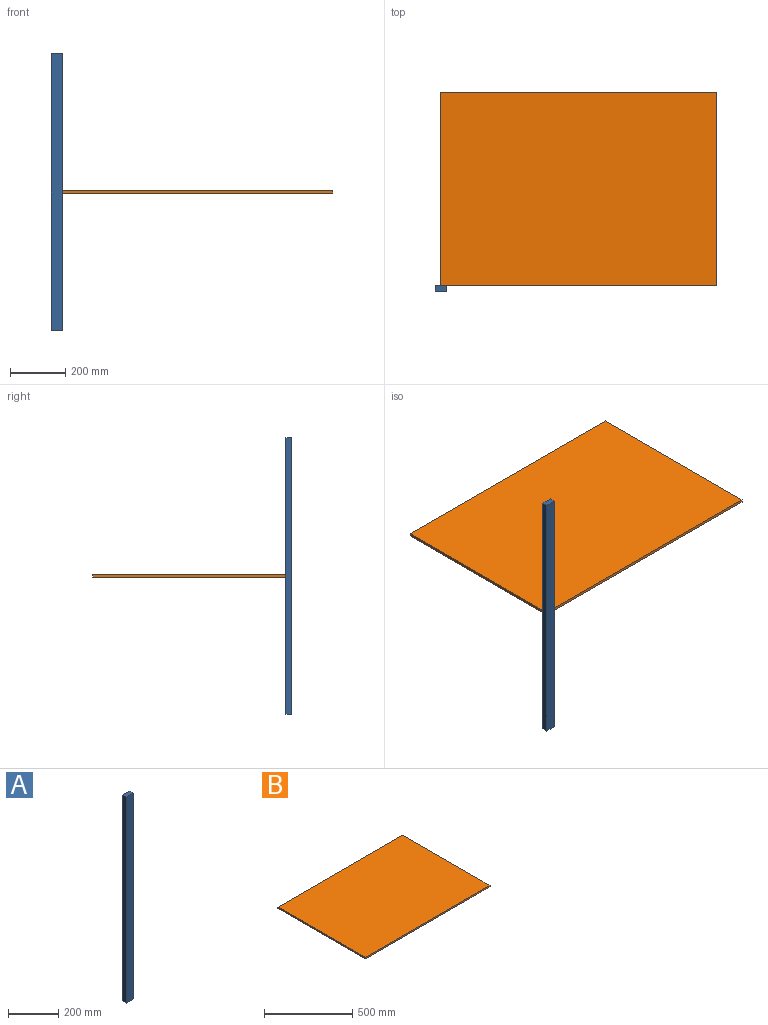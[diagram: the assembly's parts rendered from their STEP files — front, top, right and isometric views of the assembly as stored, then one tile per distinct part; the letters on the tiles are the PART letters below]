
ASSEMBLY  parts=2 mates=1
PART A: 6 faces, bbox 40x20x1000 mm
  f0: plane 1000x20mm, normal (1,0,0), area 20000mm2, adj f1,f3,f4,f5
  f1: plane 40x20mm, normal (0,0,1), area 800mm2, adj f0,f2,f4,f5
  f2: plane 1000x20mm, normal (-1,0,0), area 20000mm2, adj f1,f3,f4,f5
  f3: plane 40x20mm, normal (0,0,-1), area 800mm2, adj f0,f2,f4,f5
  f4: plane 1000x40mm, normal (0,-1,0), area 40000mm2, adj f0,f1,f2,f3
  f5: plane 1000x40mm, normal (0,1,0), area 40000mm2, adj f0,f1,f2,f3
PART B: 6 faces, bbox 1000x700x10 mm
  f0: plane 700x10mm, normal (1,0,0), area 7000mm2, adj f1,f3,f4,f5
  f1: plane 1000x10mm, normal (0,1,0), area 10000mm2, adj f0,f2,f4,f5
  f2: plane 700x10mm, normal (-1,0,0), area 7000mm2, adj f1,f3,f4,f5
  f3: plane 1000x10mm, normal (0,-1,0), area 10000mm2, adj f0,f2,f4,f5
  f4: plane 1000x700mm, normal (0,0,1), area 700000mm2, adj f0,f1,f2,f3
  f5: plane 1000x700mm, normal (0,0,-1), area 700000mm2, adj f0,f1,f2,f3
PLACE A t=(-1370.21,-708.32,124.16)mm
PLACE B t=(-870.21,-358.32,119.16)mm
MATE fastened B.f3 <-> A.f5  axis (0,-1,0) through (-1370.21,-708.32,124.16)mm
